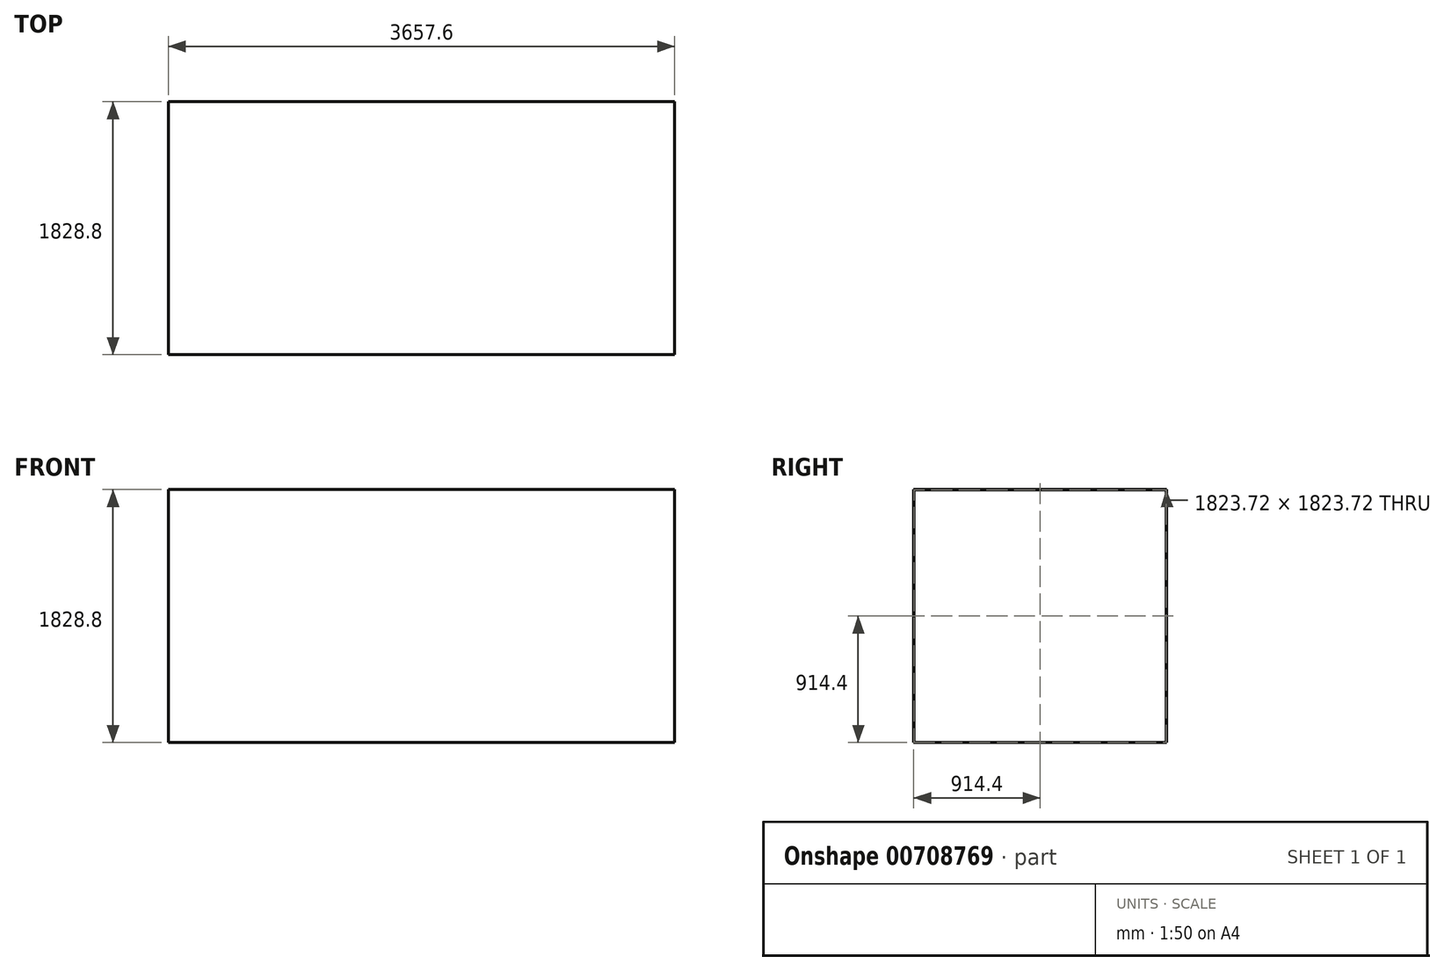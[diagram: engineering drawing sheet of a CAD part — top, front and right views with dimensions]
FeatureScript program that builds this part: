
annotation { "Feature Type Name" : "Feature", "Feature Type Description" : "" }
export const myFeature = defineFeature(function(context is Context, id is Id, definition is map)
    precondition{}
    {
        {
            var Q0;
            Q0=qCreatedBy(makeId("Front.planeOp"),FACE);
            var sketch = newSketch(context, id + "F0", { "sketchPlane" : qUnion([Q0])});
            skLineSegment(sketch, "E0.bottom", {"start": v(0, 0) * mm, "end": v(3657.6, 0) * mm});
            skLineSegment(sketch, "E0.top", {"start": v(0, 1828.8) * mm, "end": v(3657.6, 1828.8) * mm});
            skLineSegment(sketch, "E0.left", {"start": v(0, 0) * mm, "end": v(0, 1828.8) * mm});
            skLineSegment(sketch, "E0.right", {"start": v(3657.6, 0) * mm, "end": v(3657.6, 1828.8) * mm});
            skSolve(sketch);
        }
        {
            var Q0;
            Q0=makeQuery(id+"F0.imprint","IMPRINT",FACE,{"disambiguationData":[TD([[makeQuery(id+"F0.imprint","IMPRINT",EDGE,{"derivedFrom":sQuery(id+"F0.wireOp",EDGE,"E0.bottom")}),1.0]])]});
            extrude(context, id + "F1", {"entities" : qUnion([Q0]), "depth" : 1828.8 * mm, "offsetDistance" : 25.4 * mm});
        }
        {
            var Q0;
            Q0=makeQuery(id+"F1.opExtrude","SWEPT_FACE",FACE,{"disambiguationData":[OSD([sQuery(id+"F0.wireOp",EDGE,"E0.right")])]});
            var sketch = newSketch(context, id + "F2", { "sketchPlane" : qUnion([Q0])});
            skLineSegment(sketch, "E1.bottom", {"start": v(-1826.26, 2.54) * mm, "end": v(-2.54, 2.54) * mm});
            skLineSegment(sketch, "E1.top", {"start": v(-1826.26, 1826.26) * mm, "end": v(-2.54, 1826.26) * mm});
            skLineSegment(sketch, "E1.left", {"start": v(-1826.26, 2.54) * mm, "end": v(-1826.26, 1826.26) * mm});
            skLineSegment(sketch, "E1.right", {"start": v(-2.54, 2.54) * mm, "end": v(-2.54, 1826.26) * mm});
            skSolve(sketch);
        }
        {
            var Q0;
            Q0 = qSketchRegion(id + "F2", true);
            extrude(context, id + "F3", {"entities" : qUnion([Q0]), "operationType" : NewBodyOperationType.REMOVE, "endBound" : BoundingType.UP_TO_NEXT, "oppositeDirection" : true, "depth" : 25.4 * mm, "offsetDistance" : 25.4 * mm});
        }
    });
